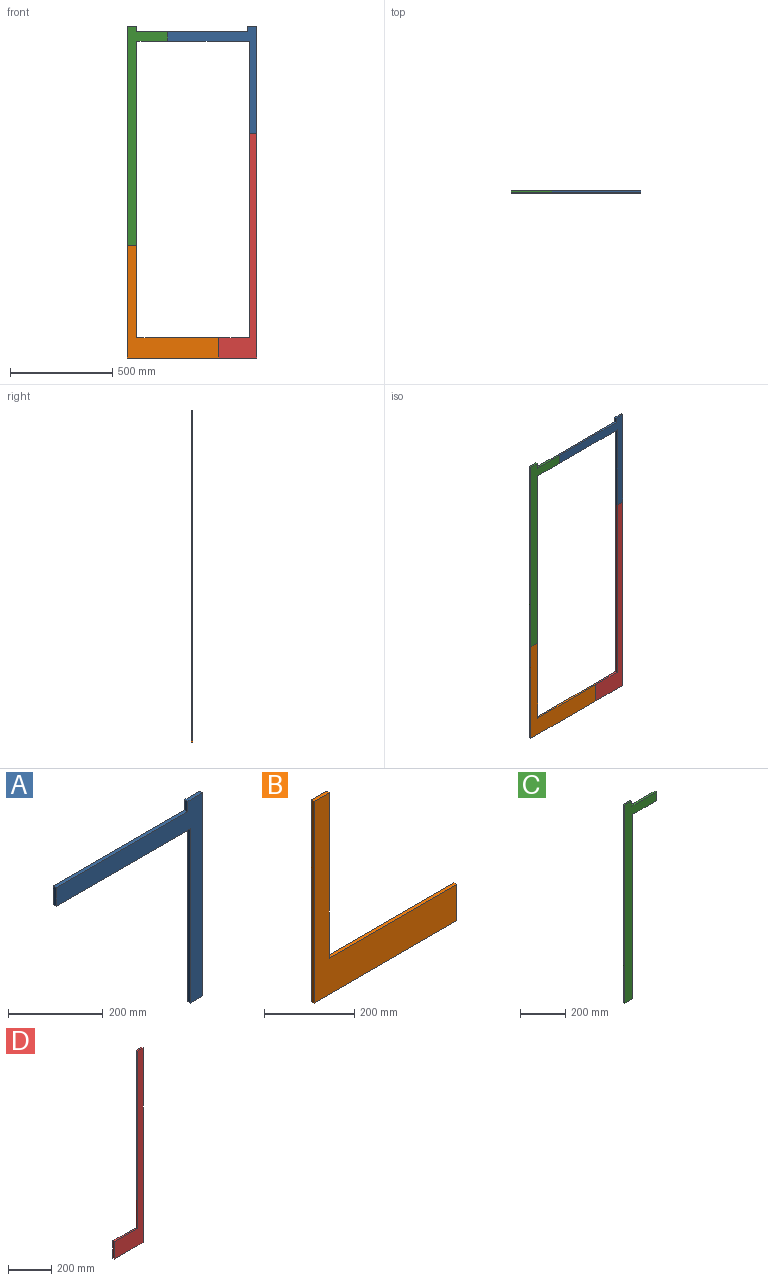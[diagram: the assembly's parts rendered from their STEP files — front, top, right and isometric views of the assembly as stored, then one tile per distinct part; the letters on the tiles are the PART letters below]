
ASSEMBLY  parts=4 mates=3
PART A: 10 faces, bbox 436.5x9x525 mm
  f0: plane 392.5x9mm, normal (0,0,1), area 3532.5mm2, adj f1,f7,f8,f9
  f1: plane 48x9mm, normal (-1,0,0), area 432mm2, adj f0,f2,f8,f9
  f2: plane 400x9mm, normal (0,0,-1), area 3600mm2, adj f1,f3,f8,f9
  f3: plane 450x9mm, normal (-1,0,0), area 4050mm2, adj f2,f4,f8,f9
  f4: plane 36.5x9mm, normal (0,0,-1), area 328.5mm2, adj f3,f5,f8,f9
  f5: plane 525x9mm, normal (1,0,0), area 4725mm2, adj f4,f6,f8,f9
  f6: plane 44x9mm, normal (0,0,1), area 396mm2, adj f5,f7,f8,f9
  f7: plane 27x9mm, normal (-1,0,0), area 243mm2, adj f0,f6,f8,f9
  f8: plane 525x436.5mm, normal (0,-1,0), area 38565mm2, adj f0,f1,f2,f3,f4,f5,f6,f7
  f9: plane 525x436.5mm, normal (0,1,0), area 38565mm2, adj f0,f1,f2,f3,f4,f5,f6,f7
PART B: 8 faces, bbox 448x9x548 mm
  f0: plane 448x9mm, normal (0,0,-1), area 4032mm2, adj f1,f5,f6,f7
  f1: plane 98x9mm, normal (1,0,0), area 882mm2, adj f0,f2,f6,f7
  f2: plane 400x9mm, normal (0,0,1), area 3600mm2, adj f1,f3,f6,f7
  f3: plane 450x9mm, normal (1,0,0), area 4050mm2, adj f2,f4,f6,f7
  f4: plane 48x9mm, normal (0,0,1), area 432mm2, adj f3,f5,f6,f7
  f5: plane 548x9mm, normal (-1,0,0), area 4932mm2, adj f0,f4,f6,f7
  f6: plane 548x448mm, normal (0,-1,0), area 65504mm2, adj f0,f1,f2,f3,f4,f5
  f7: plane 548x448mm, normal (0,1,0), area 65504mm2, adj f0,f1,f2,f3,f4,f5
PART C: 10 faces, bbox 198x9x1075 mm
  f0: plane 44x9mm, normal (0,0,1), area 396mm2, adj f1,f7,f8,f9
  f1: plane 1075x9mm, normal (-1,0,0), area 9675mm2, adj f0,f2,f8,f9
  f2: plane 48x9mm, normal (0,0,-1), area 432mm2, adj f1,f3,f8,f9
  f3: plane 1000x9mm, normal (1,0,0), area 9000mm2, adj f2,f4,f8,f9
  f4: plane 150x9mm, normal (0,0,-1), area 1350mm2, adj f3,f5,f8,f9
  f5: plane 48x9mm, normal (1,0,0), area 432mm2, adj f4,f6,f8,f9
  f6: plane 154x9mm, normal (0,0,1), area 1386mm2, adj f5,f7,f8,f9
  f7: plane 27x9mm, normal (1,0,0), area 243mm2, adj f0,f6,f8,f9
  f8: plane 1075x198mm, normal (0,-1,0), area 58692mm2, adj f0,f1,f2,f3,f4,f5,f6,f7
  f9: plane 1075x198mm, normal (0,1,0), area 58692mm2, adj f0,f1,f2,f3,f4,f5,f6,f7
PART D: 8 faces, bbox 186.5x9x1098 mm
  f0: plane 1098x9mm, normal (1,0,0), area 9882mm2, adj f1,f5,f6,f7
  f1: plane 36.5x9mm, normal (0,0,1), area 328.5mm2, adj f0,f2,f6,f7
  f2: plane 1000x9mm, normal (-1,0,0), area 9000mm2, adj f1,f3,f6,f7
  f3: plane 150x9mm, normal (0,0,1), area 1350mm2, adj f2,f4,f6,f7
  f4: plane 98x9mm, normal (-1,0,0), area 882mm2, adj f3,f5,f6,f7
  f5: plane 186.5x9mm, normal (0,0,-1), area 1678.5mm2, adj f0,f4,f6,f7
  f6: plane 1098x186.5mm, normal (0,-1,0), area 54777mm2, adj f0,f1,f2,f3,f4,f5
  f7: plane 1098x186.5mm, normal (0,1,0), area 54777mm2, adj f0,f1,f2,f3,f4,f5
PLACE A t=(-71.43,433.89,752.43)mm
PLACE B t=(178.57,433.89,-843.57)mm
PLACE C t=(-269.43,433.89,779.43)mm
PLACE D t=(365.07,433.89,254.43)mm
MATE fastened C.f8 <-> A.f8  axis (0,-1,0) through (-71.43,424.89,728.43)mm
MATE fastened D.f6 <-> B.f6  axis (0,-1,0) through (178.57,424.89,-794.57)mm
MATE fastened D.f6 <-> A.f8  axis (0,-1,0) through (346.82,424.89,254.43)mm
